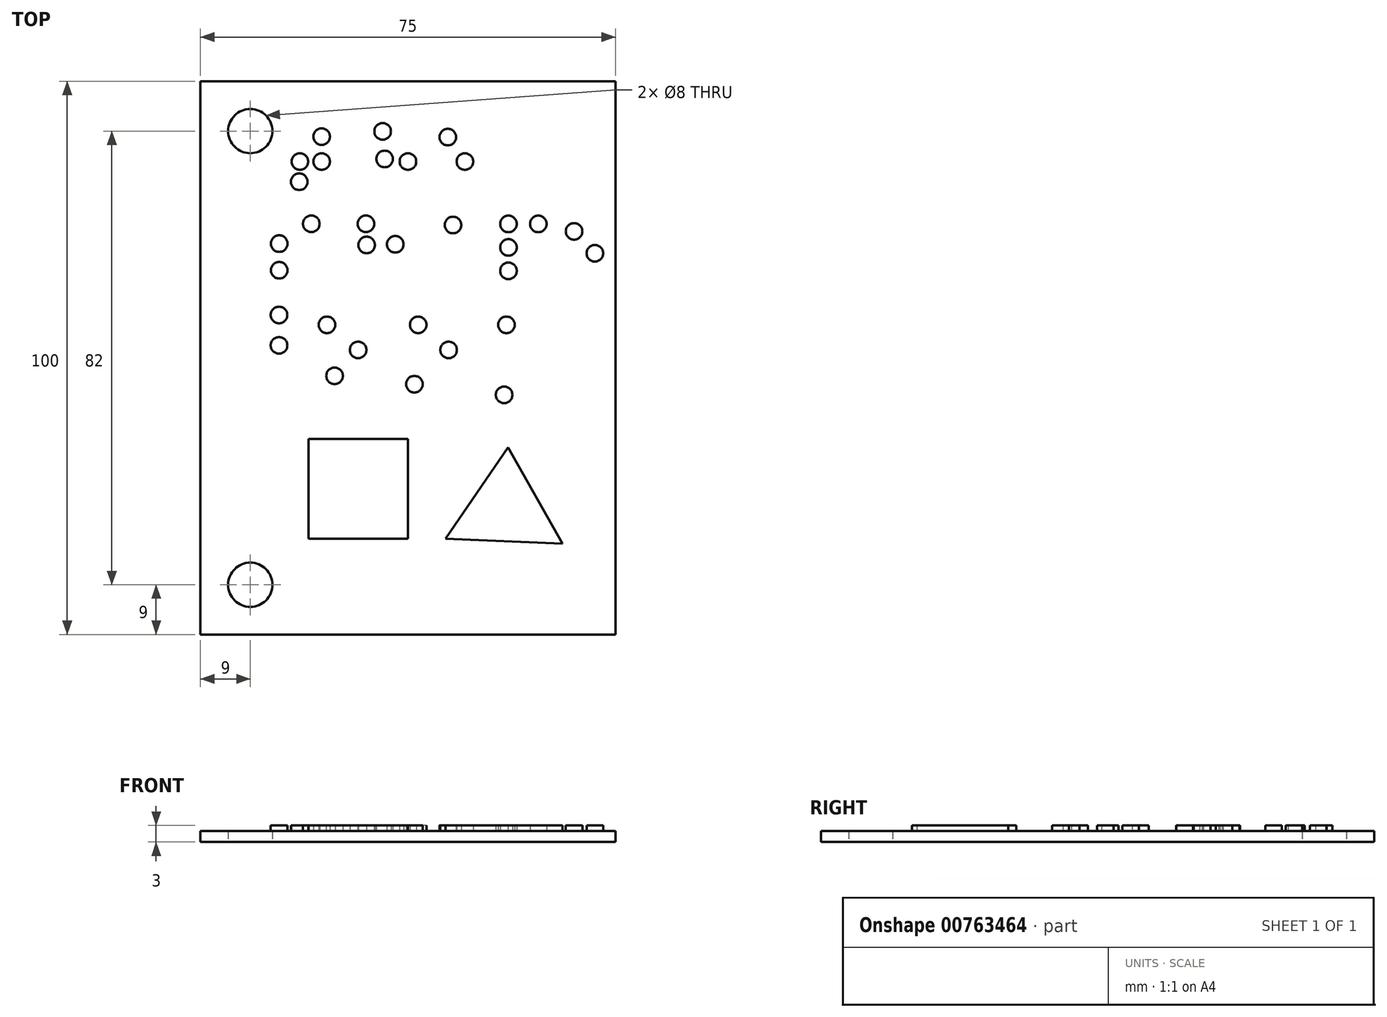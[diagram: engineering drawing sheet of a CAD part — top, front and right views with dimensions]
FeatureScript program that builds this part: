
annotation { "Feature Type Name" : "Feature", "Feature Type Description" : "" }
export const myFeature = defineFeature(function(context is Context, id is Id, definition is map)
    precondition{}
    {
        {
            var Q0;
            Q0=qCreatedBy(makeId("Top.planeOp"),FACE);
            var sketch = newSketch(context, id + "F0", { "sketchPlane" : qUnion([Q0])});
            skLineSegment(sketch, "E0.bottom", {"start": v(-37.5, 50) * mm, "end": v(37.5, 50) * mm});
            skLineSegment(sketch, "E0.top", {"start": v(-37.5, -50) * mm, "end": v(37.5, -50) * mm});
            skLineSegment(sketch, "E0.left", {"start": v(-37.5, 50) * mm, "end": v(-37.5, -50) * mm});
            skLineSegment(sketch, "E0.right", {"start": v(37.5, 50) * mm, "end": v(37.5, -50) * mm});
            skPoint(sketch, "E0.middle", {"position": v(0, 0) * mm});
            skCircle(sketch, "E1", {"center": v(-28.5, 41) * mm, "radius": 4 * mm});
            skCircle(sketch, "E2", {"center": v(-28.5, -41) * mm, "radius": 4 * mm});
            skSolve(sketch);
        }
        {
            var Q0;
            Q0 = qSketchRegion(id + "F0", true);
            extrude(context, id + "F1", {"entities" : qUnion([Q0]), "depth" : 2 * mm, "offsetDistance" : 25 * mm});
        }
        {
            var Q0;
            Q0=makeQuery(id+"F1.opExtrude","CAP_FACE",FACE,{"disambiguationData":[OSD([sQuery(id+"F0.wireOp",EDGE,"E0.bottom"),sQuery(id+"F0.wireOp",EDGE,"E0.top"),sQuery(id+"F0.wireOp",EDGE,"E0.left"),sQuery(id+"F0.wireOp",EDGE,"E0.right"),sQuery(id+"F0.wireOp",EDGE,"E1"),sQuery(id+"F0.wireOp",EDGE,"E2")])],"isStart":false});
            var sketch = newSketch(context, id + "F2", { "sketchPlane" : qUnion([Q0])});
            skCircle(sketch, "E3", {"center": v(-19.65, 31.84) * mm, "radius": 1.5 * mm});
            skCircle(sketch, "E4", {"center": v(-19.54, 35.5) * mm, "radius": 1.5 * mm});
            skCircle(sketch, "E5", {"center": v(-15.6, 35.5) * mm, "radius": 1.5 * mm});
            skCircle(sketch, "E6", {"center": v(-15.6, 40) * mm, "radius": 1.5 * mm});
            skCircle(sketch, "E7", {"center": v(0, 35.5) * mm, "radius": 1.5 * mm});
            skCircle(sketch, "E8", {"center": v(-4.2, 35.97) * mm, "radius": 1.5 * mm});
            skCircle(sketch, "E9", {"center": v(-4.57, 40.95) * mm, "radius": 1.5 * mm});
            skCircle(sketch, "E10", {"center": v(10.3, 35.5) * mm, "radius": 1.5 * mm});
            skCircle(sketch, "E11", {"center": v(7.21, 39.91) * mm, "radius": 1.5 * mm});
            skCircle(sketch, "E12", {"center": v(-23.27, 15.85) * mm, "radius": 1.5 * mm});
            skCircle(sketch, "E13", {"center": v(-23.27, 20.66) * mm, "radius": 1.5 * mm});
            skCircle(sketch, "E14", {"center": v(-17.47, 24.24) * mm, "radius": 1.5 * mm});
            skCircle(sketch, "E15", {"center": v(-7.47, 20.42) * mm, "radius": 1.5 * mm});
            skCircle(sketch, "E16", {"center": v(-2.29, 20.54) * mm, "radius": 1.5 * mm});
            skCircle(sketch, "E17", {"center": v(-7.6, 24.24) * mm, "radius": 1.5 * mm});
            skCircle(sketch, "E18", {"center": v(8.14, 24.03) * mm, "radius": 1.5 * mm});
            skCircle(sketch, "E19", {"center": v(18.17, 15.73) * mm, "radius": 1.5 * mm});
            skCircle(sketch, "E20", {"center": v(18.17, 19.98) * mm, "radius": 1.5 * mm});
            skCircle(sketch, "E21", {"center": v(18.17, 24.22) * mm, "radius": 1.5 * mm});
            skCircle(sketch, "E22", {"center": v(23.57, 24.22) * mm, "radius": 1.5 * mm});
            skCircle(sketch, "E23", {"center": v(33.8, 18.92) * mm, "radius": 1.5 * mm});
            skCircle(sketch, "E24", {"center": v(30.03, 22.87) * mm, "radius": 1.5 * mm});
            skCircle(sketch, "E25", {"center": v(-23.3, 7.77) * mm, "radius": 1.5 * mm});
            skCircle(sketch, "E26", {"center": v(-23.3, 2.27) * mm, "radius": 1.5 * mm});
            skCircle(sketch, "E27", {"center": v(-13.27, -3.23) * mm, "radius": 1.5 * mm});
            skCircle(sketch, "E28", {"center": v(-9, 1.44) * mm, "radius": 1.5 * mm});
            skCircle(sketch, "E29", {"center": v(-14.64, 5.98) * mm, "radius": 1.5 * mm});
            skCircle(sketch, "E30", {"center": v(1.86, 5.98) * mm, "radius": 1.5 * mm});
            skCircle(sketch, "E31", {"center": v(7.36, 1.44) * mm, "radius": 1.5 * mm});
            skCircle(sketch, "E32", {"center": v(1.17, -4.74) * mm, "radius": 1.5 * mm});
            skCircle(sketch, "E33", {"center": v(17.8, 5.98) * mm, "radius": 1.5 * mm});
            skCircle(sketch, "E34", {"center": v(17.4, -6.67) * mm, "radius": 1.5 * mm});
            skLineSegment(sketch, "E35.bottom", {"start": v(-18, -14.66) * mm, "end": v(0, -14.66) * mm});
            skLineSegment(sketch, "E35.top", {"start": v(-18, -32.66) * mm, "end": v(0, -32.66) * mm});
            skLineSegment(sketch, "E35.left", {"start": v(-18, -14.66) * mm, "end": v(-18, -32.66) * mm});
            skLineSegment(sketch, "E35.right", {"start": v(0, -14.66) * mm, "end": v(0, -32.66) * mm});
            skLineSegment(sketch, "E36", {"start": v(6.8, -32.66) * mm, "end": v(18.09, -16.14) * mm});
            skLineSegment(sketch, "E37", {"start": v(18.09, -16.14) * mm, "end": v(27.93, -33.55) * mm});
            skLineSegment(sketch, "E38", {"start": v(27.93, -33.55) * mm, "end": v(6.8, -32.66) * mm});
            skSolve(sketch);
        }
        {
            var Q0;
            Q0=makeQuery(id+"F2.imprint","IMPRINT",FACE,{"disambiguationData":[TD([[makeQuery(id+"F2.imprint","IMPRINT",EDGE,{"derivedFrom":sQuery(id+"F2.wireOp",EDGE,"E4")}),1.0]])]});
            var Q1;
            Q1=makeQuery(id+"F2.imprint","IMPRINT",FACE,{"disambiguationData":[TD([[makeQuery(id+"F2.imprint","IMPRINT",EDGE,{"derivedFrom":sQuery(id+"F2.wireOp",EDGE,"E5")}),1.0]])]});
            var Q2;
            Q2=makeQuery(id+"F2.imprint","IMPRINT",FACE,{"disambiguationData":[TD([[makeQuery(id+"F2.imprint","IMPRINT",EDGE,{"derivedFrom":sQuery(id+"F2.wireOp",EDGE,"E6")}),1.0]])]});
            var Q3;
            Q3=makeQuery(id+"F2.imprint","IMPRINT",FACE,{"disambiguationData":[TD([[makeQuery(id+"F2.imprint","IMPRINT",EDGE,{"derivedFrom":sQuery(id+"F2.wireOp",EDGE,"E9")}),1.0]])]});
            var Q4;
            Q4=makeQuery(id+"F2.imprint","IMPRINT",FACE,{"disambiguationData":[TD([[makeQuery(id+"F2.imprint","IMPRINT",EDGE,{"derivedFrom":sQuery(id+"F2.wireOp",EDGE,"E8")}),1.0]])]});
            var Q5;
            Q5=makeQuery(id+"F2.imprint","IMPRINT",FACE,{"disambiguationData":[TD([[makeQuery(id+"F2.imprint","IMPRINT",EDGE,{"derivedFrom":sQuery(id+"F2.wireOp",EDGE,"E7")}),1.0]])]});
            var Q6;
            Q6=makeQuery(id+"F2.imprint","IMPRINT",FACE,{"disambiguationData":[TD([[makeQuery(id+"F2.imprint","IMPRINT",EDGE,{"derivedFrom":sQuery(id+"F2.wireOp",EDGE,"E3")}),1.0]])]});
            var Q7;
            Q7=makeQuery(id+"F2.imprint","IMPRINT",FACE,{"disambiguationData":[TD([[makeQuery(id+"F2.imprint","IMPRINT",EDGE,{"derivedFrom":sQuery(id+"F2.wireOp",EDGE,"E11")}),1.0]])]});
            var Q8;
            Q8=makeQuery(id+"F2.imprint","IMPRINT",FACE,{"disambiguationData":[TD([[makeQuery(id+"F2.imprint","IMPRINT",EDGE,{"derivedFrom":sQuery(id+"F2.wireOp",EDGE,"E10")}),1.0]])]});
            var Q9;
            Q9=makeQuery(id+"F2.imprint","IMPRINT",FACE,{"disambiguationData":[TD([[makeQuery(id+"F2.imprint","IMPRINT",EDGE,{"derivedFrom":sQuery(id+"F2.wireOp",EDGE,"E24")}),1.0]])]});
            var Q10;
            Q10=makeQuery(id+"F2.imprint","IMPRINT",FACE,{"disambiguationData":[TD([[makeQuery(id+"F2.imprint","IMPRINT",EDGE,{"derivedFrom":sQuery(id+"F2.wireOp",EDGE,"E23")}),1.0]])]});
            var Q11;
            Q11=makeQuery(id+"F2.imprint","IMPRINT",FACE,{"disambiguationData":[TD([[makeQuery(id+"F2.imprint","IMPRINT",EDGE,{"derivedFrom":sQuery(id+"F2.wireOp",EDGE,"E22")}),1.0]])]});
            var Q12;
            Q12=makeQuery(id+"F2.imprint","IMPRINT",FACE,{"disambiguationData":[TD([[makeQuery(id+"F2.imprint","IMPRINT",EDGE,{"derivedFrom":sQuery(id+"F2.wireOp",EDGE,"E21")}),1.0]])]});
            var Q13;
            Q13=makeQuery(id+"F2.imprint","IMPRINT",FACE,{"disambiguationData":[TD([[makeQuery(id+"F2.imprint","IMPRINT",EDGE,{"derivedFrom":sQuery(id+"F2.wireOp",EDGE,"E20")}),1.0]])]});
            var Q14;
            Q14=makeQuery(id+"F2.imprint","IMPRINT",FACE,{"disambiguationData":[TD([[makeQuery(id+"F2.imprint","IMPRINT",EDGE,{"derivedFrom":sQuery(id+"F2.wireOp",EDGE,"E19")}),1.0]])]});
            var Q15;
            Q15=makeQuery(id+"F2.imprint","IMPRINT",FACE,{"disambiguationData":[TD([[makeQuery(id+"F2.imprint","IMPRINT",EDGE,{"derivedFrom":sQuery(id+"F2.wireOp",EDGE,"E18")}),1.0]])]});
            var Q16;
            Q16=makeQuery(id+"F2.imprint","IMPRINT",FACE,{"disambiguationData":[TD([[makeQuery(id+"F2.imprint","IMPRINT",EDGE,{"derivedFrom":sQuery(id+"F2.wireOp",EDGE,"E16")}),1.0]])]});
            var Q17;
            Q17=makeQuery(id+"F2.imprint","IMPRINT",FACE,{"disambiguationData":[TD([[makeQuery(id+"F2.imprint","IMPRINT",EDGE,{"derivedFrom":sQuery(id+"F2.wireOp",EDGE,"E15")}),1.0]])]});
            var Q18;
            Q18=makeQuery(id+"F2.imprint","IMPRINT",FACE,{"disambiguationData":[TD([[makeQuery(id+"F2.imprint","IMPRINT",EDGE,{"derivedFrom":sQuery(id+"F2.wireOp",EDGE,"E17")}),1.0]])]});
            var Q19;
            Q19=makeQuery(id+"F2.imprint","IMPRINT",FACE,{"disambiguationData":[TD([[makeQuery(id+"F2.imprint","IMPRINT",EDGE,{"derivedFrom":sQuery(id+"F2.wireOp",EDGE,"E14")}),1.0]])]});
            var Q20;
            Q20=makeQuery(id+"F2.imprint","IMPRINT",FACE,{"disambiguationData":[TD([[makeQuery(id+"F2.imprint","IMPRINT",EDGE,{"derivedFrom":sQuery(id+"F2.wireOp",EDGE,"E13")}),1.0]])]});
            var Q21;
            Q21=makeQuery(id+"F2.imprint","IMPRINT",FACE,{"disambiguationData":[TD([[makeQuery(id+"F2.imprint","IMPRINT",EDGE,{"derivedFrom":sQuery(id+"F2.wireOp",EDGE,"E12")}),1.0]])]});
            var Q22;
            Q22=makeQuery(id+"F2.imprint","IMPRINT",FACE,{"disambiguationData":[TD([[makeQuery(id+"F2.imprint","IMPRINT",EDGE,{"derivedFrom":sQuery(id+"F2.wireOp",EDGE,"E25")}),1.0]])]});
            var Q23;
            Q23=makeQuery(id+"F2.imprint","IMPRINT",FACE,{"disambiguationData":[TD([[makeQuery(id+"F2.imprint","IMPRINT",EDGE,{"derivedFrom":sQuery(id+"F2.wireOp",EDGE,"E26")}),1.0]])]});
            var Q24;
            Q24=makeQuery(id+"F2.imprint","IMPRINT",FACE,{"disambiguationData":[TD([[makeQuery(id+"F2.imprint","IMPRINT",EDGE,{"derivedFrom":sQuery(id+"F2.wireOp",EDGE,"E29")}),1.0]])]});
            var Q25;
            Q25=makeQuery(id+"F2.imprint","IMPRINT",FACE,{"disambiguationData":[TD([[makeQuery(id+"F2.imprint","IMPRINT",EDGE,{"derivedFrom":sQuery(id+"F2.wireOp",EDGE,"E28")}),1.0]])]});
            var Q26;
            Q26=makeQuery(id+"F2.imprint","IMPRINT",FACE,{"disambiguationData":[TD([[makeQuery(id+"F2.imprint","IMPRINT",EDGE,{"derivedFrom":sQuery(id+"F2.wireOp",EDGE,"E27")}),1.0]])]});
            var Q27;
            Q27=makeQuery(id+"F2.imprint","IMPRINT",FACE,{"disambiguationData":[TD([[makeQuery(id+"F2.imprint","IMPRINT",EDGE,{"derivedFrom":sQuery(id+"F2.wireOp",EDGE,"E30")}),1.0]])]});
            var Q28;
            Q28=makeQuery(id+"F2.imprint","IMPRINT",FACE,{"disambiguationData":[TD([[makeQuery(id+"F2.imprint","IMPRINT",EDGE,{"derivedFrom":sQuery(id+"F2.wireOp",EDGE,"E31")}),1.0]])]});
            var Q29;
            Q29=makeQuery(id+"F2.imprint","IMPRINT",FACE,{"disambiguationData":[TD([[makeQuery(id+"F2.imprint","IMPRINT",EDGE,{"derivedFrom":sQuery(id+"F2.wireOp",EDGE,"E32")}),1.0]])]});
            var Q30;
            Q30=makeQuery(id+"F2.imprint","IMPRINT",FACE,{"disambiguationData":[TD([[makeQuery(id+"F2.imprint","IMPRINT",EDGE,{"derivedFrom":sQuery(id+"F2.wireOp",EDGE,"E34")}),1.0]])]});
            var Q31;
            Q31=makeQuery(id+"F2.imprint","IMPRINT",FACE,{"disambiguationData":[TD([[makeQuery(id+"F2.imprint","IMPRINT",EDGE,{"derivedFrom":sQuery(id+"F2.wireOp",EDGE,"E33")}),1.0]])]});
            var Q32;
            Q32=makeQuery(id+"F2.imprint","IMPRINT",FACE,{"disambiguationData":[TD([[makeQuery(id+"F2.imprint","IMPRINT",EDGE,{"derivedFrom":sQuery(id+"F2.wireOp",EDGE,"E36")}),-1.0]])]});
            var Q33;
            Q33=makeQuery(id+"F2.imprint","IMPRINT",FACE,{"disambiguationData":[TD([[makeQuery(id+"F2.imprint","IMPRINT",EDGE,{"derivedFrom":sQuery(id+"F2.wireOp",EDGE,"E35.bottom")}),-1.0]])]});
            extrude(context, id + "F3", {"entities" : qUnion([Q0, Q1, Q2, Q3, Q4, Q5, Q6, Q7, Q8, Q9, Q10, Q11, Q12, Q13, Q14, Q15, Q16, Q17, Q18, Q19, Q20, Q21, Q22, Q23, Q24, Q25, Q26, Q27, Q28, Q29, Q30, Q31, Q32, Q33]), "operationType" : NewBodyOperationType.ADD, "depth" : 1 * mm, "offsetDistance" : 25 * mm});
        }
    });
